# Revit family: FU_Modular_Sandler_Charlotte 111
name_source: partatom
category: Furniture
units: mm (PartAtom-declared; Revit-internal decimal feet)

## family parameters
Always vertical = Yes
Cut with Voids When Loaded = No
OmniClass Number = 23.40.20.00
OmniClass Title = General Furniture and Specialties
Render Appearance Source = Family Geometry
Room Calculation Point = No
Shared = No
Work Plane-Based = No

## types (1)
- Charlotte 111
    Default Elevation = 0 mm  [stored 0 ft]
    Depth = 660 mm  [stored 2.16535 ft]
    Description = Long rectangular ottoman in the Charlotte modular seating series. Made in the U.S.
    Height = 440 mm  [stored 1.44357 ft]
    Manufacturer = Sandler
    Model = Charlotte 111
    URL = https://www.sandlerseating.com
    Width = 1360 mm  [stored 4.46194 ft]

note: [stored X ft] marks values corroborated as IEEE doubles in the binary element streams (Revit-internal decimal feet)

## geometry (parser evidence)
native form markers: Sweep x5
no freeform markers — native parametric forms only
